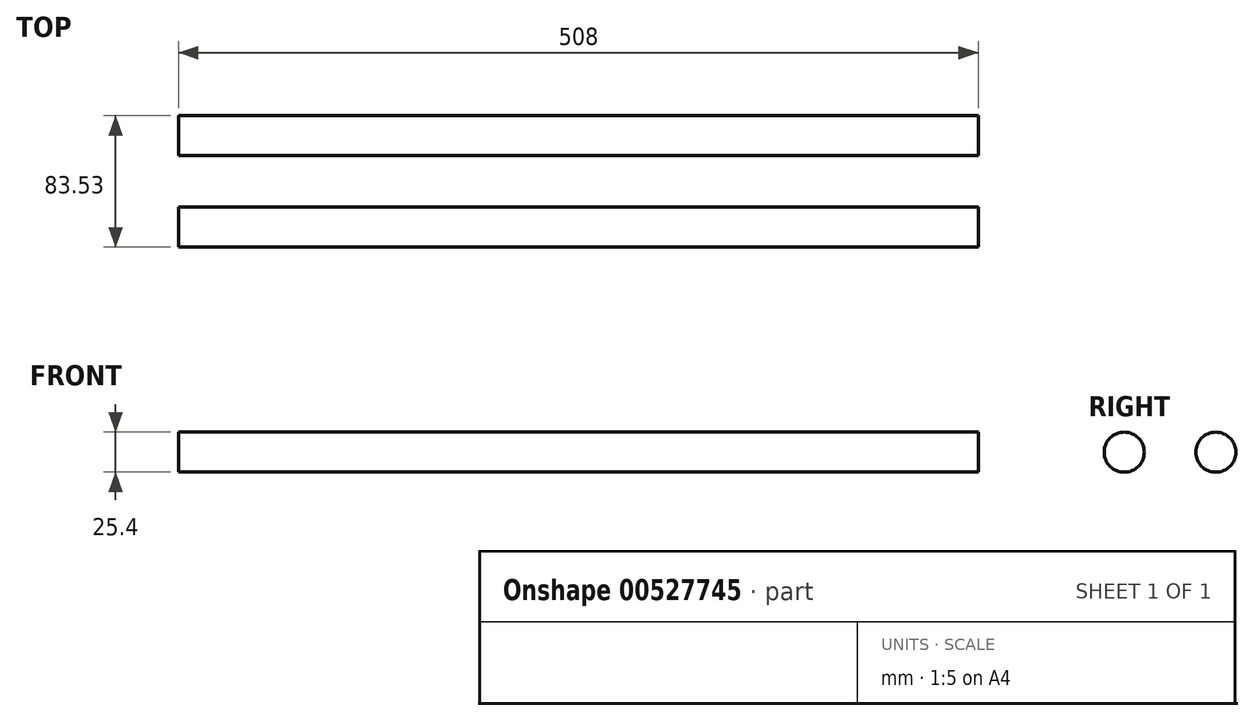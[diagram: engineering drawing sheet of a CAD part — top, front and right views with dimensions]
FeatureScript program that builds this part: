
annotation { "Feature Type Name" : "Feature", "Feature Type Description" : "" }
export const myFeature = defineFeature(function(context is Context, id is Id, definition is map)
    precondition{}
    {
        {
            var Q0;
            Q0=qCreatedBy(makeId("Right.planeOp"),FACE);
            var sketch = newSketch(context, id + "F0", { "sketchPlane" : qUnion([Q0])});
            skCircle(sketch, "E0", {"center": v(0, 0) * mm, "radius": 12.7 * mm});
            skCircle(sketch, "E1", {"center": v(58.13, 0) * mm, "radius": 12.7 * mm});
            skSolve(sketch);
        }
        {
            var Q0;
            Q0=makeQuery(id+"F0.imprint","IMPRINT",FACE,{"disambiguationData":[TD([[makeQuery(id+"F0.imprint","IMPRINT",EDGE,{"derivedFrom":sQuery(id+"F0.wireOp",EDGE,"E1")}),1.0]])]});
            var Q1;
            Q1=makeQuery(id+"F0.imprint","IMPRINT",FACE,{"disambiguationData":[TD([[makeQuery(id+"F0.imprint","IMPRINT",EDGE,{"derivedFrom":sQuery(id+"F0.wireOp",EDGE,"E0")}),1.0]])]});
            extrude(context, id + "F1", {"entities" : qUnion([Q0, Q1]), "depth" : 508 * mm, "offsetDistance" : 25.4 * mm});
        }
    });
